# Revit family: CONVO LILY PAD & CART COMBO
name_source: partatom
category: Furniture Systems
units: mm (PartAtom-declared; Revit-internal decimal feet)

## family parameters
Always vertical = Yes
Cut with Voids When Loaded = No
Part Type = Normal
Room Calculation Point = No
Round Connector Dimension = Use Diameter
Shared = No
Work Plane-Based = No

## types (2) — shared parameters
3" Lily pad Fabric-1 = <By Category>
3" Lily pad Fabric-10 = <By Category>
3" Lily pad Fabric-2 = <By Category>
3" Lily pad Fabric-3 = <By Category>
3" Lily pad Fabric-4 = <By Category>
3" Lily pad Fabric-5 = <By Category>
3" Lily pad Fabric-6 = <By Category>
3" Lily pad Fabric-7 = <By Category>
3" Lily pad Fabric-8 = <By Category>
3" Lily pad Fabric-9 = <By Category>
6" Lily pad Fabric-1 = <By Category>
6" Lily pad Fabric-2 = <By Category>
6" Lily pad Fabric-3 = <By Category>
6" Lily pad Fabric-4 = <By Category>
6" Lily pad Fabric-5 = <By Category>
6" Lily pad Fabric-6 = <By Category>
Caster = Black
Frame = <By Category>
Lily Cart = FK007-CART2
Manufacturer = FOMCORE
Model = CONVO LILY PAD & CART COMBO
URL = https://fomcore.com

## per-type parameters (varying)
| type | 3" Lily Pad | 3" Lily pad | 3" PAD | 6" Lily Pad | 6" Lily pad | 6" PAD | Description |
| Cart with 3" Lily Pad | FK007-18x3 | Yes | 1 | - | No | 0 | Combo Products - Convo lily pad & cart combo |
| Cart with 6" Lily Pad | - | No | 0 | FK007-18x6 | Yes | 2 | Combo Products - CONVO LILY PAD & CART COMBO |

## geometry (parser evidence)
native form markers: Sweep x2
no freeform markers — native parametric forms only
